# Revit family: Desk_Accessories-Teknion-BAMPL_Peninsula_Modesty_Panel_Solid-R2018
name_source: partatom
category: Furniture
revit_build: Autodesk Revit 2018 (Build: 20190510_1515(x64)
units: mm (PartAtom-declared; Revit-internal decimal feet)

## family parameters
Always vertical = Yes
Cut with Voids When Loaded = No
OmniClass Number = 23.40.20.00
OmniClass Title = General Furniture and Specialties
Room Calculation Point = No
Shared = Yes
Work Plane-Based = No

## types (3) — shared parameters
Assembly Code = E2020200
Manufacturer = Teknion
Manufacturer Fax = 416.661.4586
Part Number = BAMPL
Product Documentation Link = https://www.teknion.com
Product Line = Expansion Casegoods
Product Page URL = https://www.teknion.com
Series = Expansion Casegoods
Sustainability Data = https://www.teknion.com
URL = www.teknion.com
Unit Weight URL = http://www.teknion.com
Warranty = http://www.teknion.com

## per-type parameters (varying)
| type | Description | Dual Leg | Model | Modesty Panel Height |
| Dual-Leg Peninsula Style, Half Modesty Panel Height | Peninsula Modesty Panel – Solid, Dual-Leg Peninsula Style, Half Modesty Panel Height | Yes | BAMPLDH__ | 11 " |
| Mono-Leg or Base Peninsula Style, Full Modesty Panel Height | Peninsula Modesty Panel – Solid, Mono-Leg or Base Peninsula Style, Full Modesty Panel Height | No | BAMPLMF__ | 26.933 " |
| Mono-Leg or Base Peninsula Style, Half Modesty Panel Height | Peninsula Modesty Panel – Solid, Mono-Leg or Base Peninsula Style, Half Modesty Panel Height | No | BAMPLMH__ | 11 " |

## geometry (parser evidence)
native form markers: Blend x1, Sweep x3
no freeform markers — native parametric forms only
